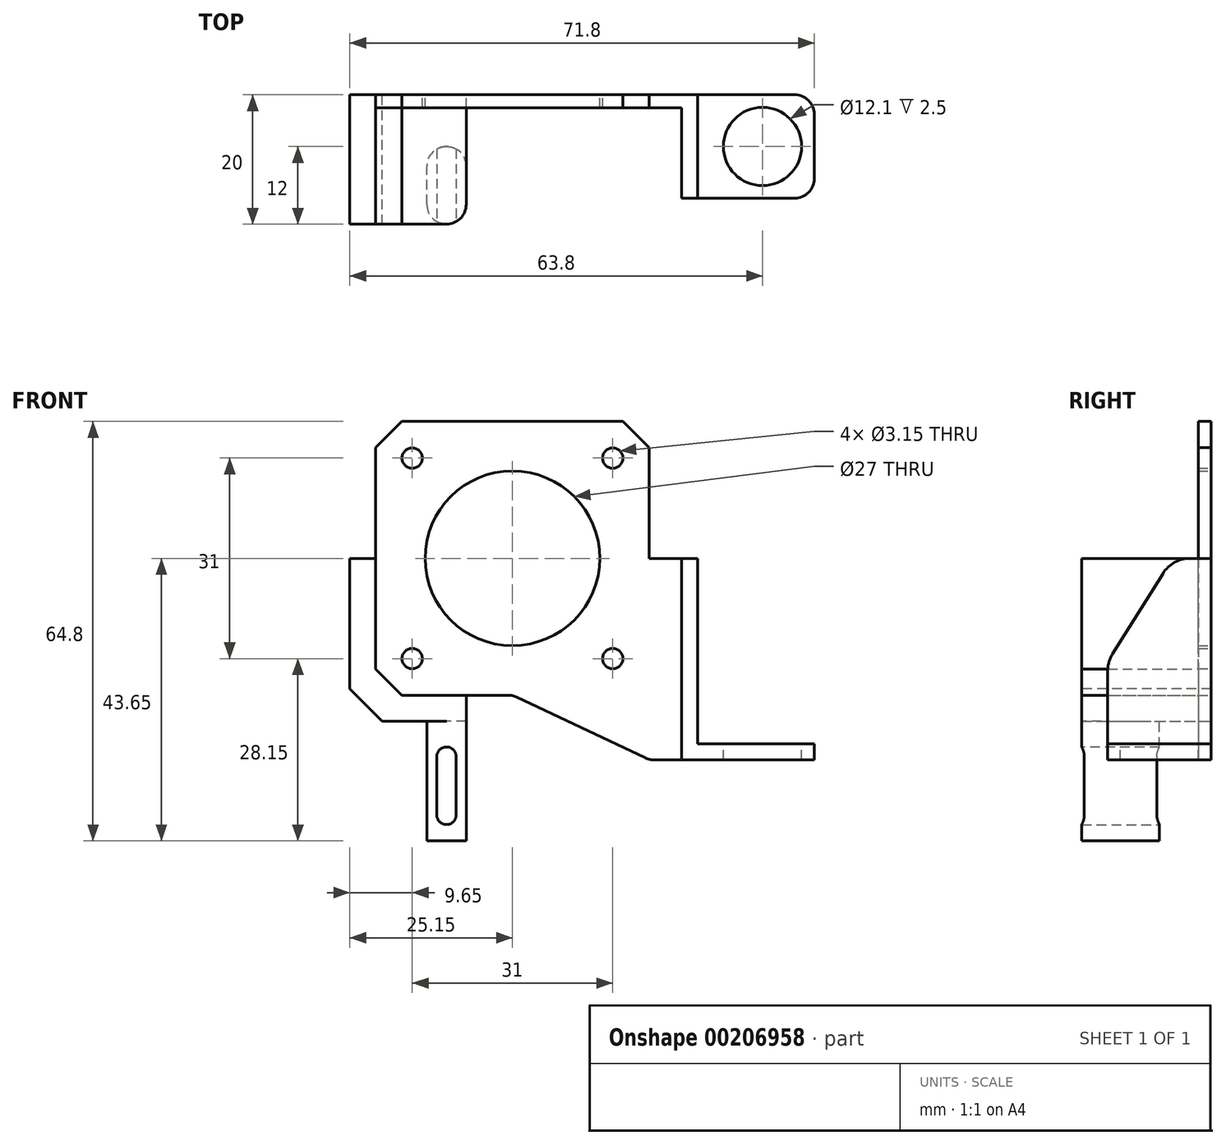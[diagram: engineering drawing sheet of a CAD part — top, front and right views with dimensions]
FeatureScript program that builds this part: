
annotation { "Feature Type Name" : "Feature", "Feature Type Description" : "" }
export const myFeature = defineFeature(function(context is Context, id is Id, definition is map)
    precondition{}
    {
        {
            var Q0;
            Q0=qCreatedBy(makeId("Front.planeOp"),FACE);
            var sketch = newSketch(context, id + "F0", { "sketchPlane" : qUnion([Q0])});
            skLineSegment(sketch, "E0.bottom", {"start": v(21.15, 21.15) * mm, "end": v(-21.15, 21.15) * mm});
            skLineSegment(sketch, "E0.top", {"start": v(21.15, -21.15) * mm, "end": v(-21.15, -21.15) * mm});
            skLineSegment(sketch, "E0.left", {"start": v(21.15, 21.15) * mm, "end": v(21.15, -21.15) * mm});
            skLineSegment(sketch, "E0.right", {"start": v(-21.15, 21.15) * mm, "end": v(-21.15, -21.15) * mm});
            skPoint(sketch, "E0.middle", {"position": v(0, 0) * mm});
            skCircle(sketch, "E1", {"center": v(0, 0) * mm, "radius": 13.5 * mm});
            skCircle(sketch, "E2", {"center": v(-15.5, 15.5) * mm, "radius": 1.57 * mm});
            skCircle(sketch, "E3.MirrorC", {"center": v(15.5, 15.5) * mm, "radius": 1.57 * mm});
            skCircle(sketch, "E4.MirrorC", {"center": v(-15.5, -15.5) * mm, "radius": 1.57 * mm});
            skCircle(sketch, "E5.MirrorC", {"center": v(15.5, -15.5) * mm, "radius": 1.57 * mm});
            skLineSegment(sketch, "E6", {"start": v(-21.15, 0) * mm, "end": v(-25.15, 0) * mm});
            skLineSegment(sketch, "E7", {"start": v(-25.15, 0) * mm, "end": v(-25.15, -25.15) * mm});
            skLineSegment(sketch, "E8", {"start": v(-7.15, -21.15) * mm, "end": v(-7.15, -25.15) * mm});
            skLineSegment(sketch, "E9", {"start": v(-17.08, 21.15) * mm, "end": v(-21.15, 17.08) * mm});
            skLineSegment(sketch, "E10.MirrorCS", {"start": v(17.08, 21.15) * mm, "end": v(21.15, 17.08) * mm});
            skLineSegment(sketch, "E11", {"start": v(-25.15, -25.15) * mm, "end": v(-7.15, -25.15) * mm});
            skLineSegment(sketch, "E12.MirrorCS", {"start": v(-17.08, -21.15) * mm, "end": v(-21.15, -17.08) * mm});
            skLineSegment(sketch, "E13", {"start": v(0, -21.15) * mm, "end": v(21.2, -31.15) * mm});
            skLineSegment(sketch, "E14", {"start": v(21.2, -31.15) * mm, "end": v(46.65, -31.15) * mm});
            skLineSegment(sketch, "E15", {"start": v(46.65, -31.15) * mm, "end": v(46.65, -28.65) * mm});
            skLineSegment(sketch, "E16", {"start": v(46.65, -28.65) * mm, "end": v(28.65, -28.65) * mm});
            skLineSegment(sketch, "E17", {"start": v(28.65, -28.65) * mm, "end": v(28.65, 0) * mm});
            skLineSegment(sketch, "E18", {"start": v(21.15, 0) * mm, "end": v(28.65, 0) * mm});
            skLineSegment(sketch, "E19", {"start": v(26.15, -31.15) * mm, "end": v(26.15, 0) * mm});
            skLineSegment(sketch, "E20", {"start": v(21.15, -21.15) * mm, "end": v(26.15, -21.15) * mm});
            skSolve(sketch);
        }
        {
            var Q0;
            {var subQ1=sQuery(id+"F0.wireOp",EDGE,"wdIhQOyr-LbOw-H7ru-rsnz-cjuyuC4DagCl");Q0=makeQuery(id+"F0.imprint","IMPRINT",FACE,{"disambiguationData":[TD([[makeQuery(id+"F0.imprint","IMPRINT",EDGE,{"derivedFrom":subQ1}),1.0]])]});}
            var Q1;
            {var subQ6=sQuery(id+"F0.wireOp",EDGE,"E6");Q1=makeQuery(id+"F0.imprint","IMPRINT",FACE,{"disambiguationData":[TD([[makeQuery(id+"F0.imprint","IMPRINT",EDGE,{"derivedFrom":subQ6}),1.0]])]});}
            var Q2;
            {var subQ3=sQuery(id+"F0.wireOp",EDGE,"GB1PjnFZ-qV7y-NF51-fnbe-eRyrRNSTYp6C");Q2=makeQuery(id+"F0.imprint","IMPRINT",FACE,{"disambiguationData":[TD([[makeQuery(id+"F0.imprint","IMPRINT",EDGE,{"derivedFrom":subQ3}),1.0]])]});}
            var Q3;
            Q3=makeQuery(id+"F0.imprint","IMPRINT",FACE,{"disambiguationData":[TD([[makeQuery(id+"F0.imprint","IMPRINT",EDGE,{"derivedFrom":sQuery(id+"F0.wireOp",EDGE,"E1")}),-1.0]])]});
            var Q4;
            {var subQ3=sQuery(id+"F0.wireOp",EDGE,"E12.MirrorCS");Q4=makeQuery(id+"F0.imprint","IMPRINT",FACE,{"disambiguationData":[TD([[makeQuery(id+"F0.imprint","IMPRINT",EDGE,{"derivedFrom":subQ3}),1.0]])]});}
            var Q5;
            {var subQ1=sQuery(id+"F0.wireOp",EDGE,"E13");Q5=makeQuery(id+"F0.imprint","IMPRINT",FACE,{"disambiguationData":[TD([[makeQuery(id+"F0.imprint","IMPRINT",EDGE,{"derivedFrom":subQ1}),1.0]])]});}
            var Q6;
            {var subQ1=sQuery(id+"F0.wireOp",EDGE,"E15");Q6=makeQuery(id+"F0.imprint","IMPRINT",FACE,{"disambiguationData":[TD([[makeQuery(id+"F0.imprint","IMPRINT",EDGE,{"derivedFrom":subQ1}),1.0]])]});}
            var Q7;
            {var subQ0=sQuery(id+"F0.wireOp",EDGE,"E20");Q7=makeQuery(id+"F0.imprint","IMPRINT",FACE,{"disambiguationData":[TD([[makeQuery(id+"F0.imprint","IMPRINT",EDGE,{"derivedFrom":subQ0}),1.0]])]});}
            extrude(context, id + "F1", {"entities" : qUnion([Q0, Q1, Q2, Q3, Q4, Q5, Q6, Q7]), "depth" : 2 * mm});
        }
        {
            var Q0;
            {var subQ6=sQuery(id+"F0.wireOp",EDGE,"E6");Q0=makeQuery(id+"F0.imprint","IMPRINT",FACE,{"disambiguationData":[TD([[makeQuery(id+"F0.imprint","IMPRINT",EDGE,{"derivedFrom":subQ6}),1.0]])]});}
            var Q1;
            {var subQ3=sQuery(id+"F0.wireOp",EDGE,"E12.MirrorCS");Q1=makeQuery(id+"F0.imprint","IMPRINT",FACE,{"disambiguationData":[TD([[makeQuery(id+"F0.imprint","IMPRINT",EDGE,{"derivedFrom":subQ3}),1.0]])]});}
            extrude(context, id + "F2", {"entities" : qUnion([Q0, Q1]), "operationType" : NewBodyOperationType.ADD, "depth" : 20 * mm});
        }
        {
            var Q0;
            {var subQ1=sQuery(id+"F0.wireOp",EDGE,"E15");Q0=makeQuery(id+"F0.imprint","IMPRINT",FACE,{"disambiguationData":[TD([[makeQuery(id+"F0.imprint","IMPRINT",EDGE,{"derivedFrom":subQ1}),1.0]])]});}
            extrude(context, id + "F3", {"entities" : qUnion([Q0]), "operationType" : NewBodyOperationType.ADD, "depth" : 16 * mm});
        }
        {
            var Q0;
            {var subQ0=sQuery(id+"F0.wireOp",EDGE,"E16");Q0=makeQuery(id+"F3.boolean.opBoolean","MERGE",FACE,{"derivedFrom":[makeQuery(id+"F1.opExtrude","SWEPT_FACE",FACE,{"disambiguationData":[OSD([subQ0])]}),makeQuery(id+"F3.opExtrude","SWEPT_FACE",FACE,{"disambiguationData":[OSD([subQ0])]})]});}
            var sketch = newSketch(context, id + "F4", { "sketchPlane" : qUnion([Q0])});
            skCircle(sketch, "E21", {"center": v(38.65, -8) * mm, "radius": 6.05 * mm});
            skSolve(sketch);
        }
        {
            var Q0;
            Q0 = qSketchRegion(id + "F4", true);
            extrude(context, id + "F5", {"entities" : qUnion([Q0]), "operationType" : NewBodyOperationType.REMOVE, "endBound" : BoundingType.UP_TO_NEXT, "oppositeDirection" : true, "depth" : 25 * mm});
        }
        {
            var Q0;
            {var subQ0=sQuery(id+"F0.wireOp",EDGE,"E11");Q0=makeQuery(id+"F2.boolean.opBoolean","MERGE",FACE,{"derivedFrom":[makeQuery(id+"F1.opExtrude","SWEPT_FACE",FACE,{"disambiguationData":[OSD([subQ0])]}),makeQuery(id+"F2.opExtrude","SWEPT_FACE",FACE,{"disambiguationData":[OSD([subQ0])]})]});}
            var sketch = newSketch(context, id + "F6", { "sketchPlane" : qUnion([Q0])});
            skLineSegment(sketch, "E22", {"start": v(-13.25, 20) * mm, "end": v(-13.25, 8) * mm});
            skLineSegment(sketch, "E23", {"start": v(-13.25, 8) * mm, "end": v(-7.15, 8) * mm});
            skSolve(sketch);
        }
        {
            var Q0;
            Q0 = qSketchRegion(id + "F6", true);
            var Q1;
            {var subQ0=sQuery(id+"F6.wireOp",EDGE,"E22");Q1=makeQuery(id+"F6.imprint","IMPRINT",FACE,{"disambiguationData":[TD([[makeQuery(id+"F6.imprint","IMPRINT",EDGE,{"derivedFrom":subQ0}),1.0]])]});}
            extrude(context, id + "F7", {"entities" : qUnion([Q0, Q1]), "operationType" : NewBodyOperationType.ADD, "depth" : 18.5 * mm});
        }
        {
            var Q0;
            {var subQ0=sQuery(id+"F0.wireOp",EDGE,"E11");Q0=makeQuery(id+"F7.boolean.opBoolean","MERGE",FACE,{"derivedFrom":[makeQuery(id+"F2.opExtrude","CAP_FACE",FACE,{"disambiguationData":[OSD([sQuery(id+"F0.wireOp",EDGE,"E0.top"),sQuery(id+"F0.wireOp",EDGE,"E0.right"),sQuery(id+"F0.wireOp",EDGE,"E6"),sQuery(id+"F0.wireOp",EDGE,"E7"),sQuery(id+"F0.wireOp",EDGE,"E8"),subQ0,sQuery(id+"F0.wireOp",EDGE,"E12.MirrorCS")])],"isStart":false}),makeQuery(id+"F7.opExtrude","SWEPT_FACE",FACE,{"disambiguationData":[OSD([subQ0])]})]});}
            var sketch = newSketch(context, id + "F8", { "sketchPlane" : qUnion([Q0])});
            skLineSegment(sketch, "E24.bottom", {"start": v(-11.7, -29.15) * mm, "end": v(-8.7, -29.15) * mm});
            skLineSegment(sketch, "E24.top", {"start": v(-11.7, -41.15) * mm, "end": v(-8.7, -41.15) * mm});
            skLineSegment(sketch, "E24.left", {"start": v(-11.7, -29.15) * mm, "end": v(-11.7, -41.15) * mm});
            skLineSegment(sketch, "E24.right", {"start": v(-8.7, -29.15) * mm, "end": v(-8.7, -41.15) * mm});
            skSolve(sketch);
        }
        {
            var Q0;
            Q0 = qSketchRegion(id + "F8", true);
            extrude(context, id + "F9", {"entities" : qUnion([Q0]), "operationType" : NewBodyOperationType.REMOVE, "endBound" : BoundingType.UP_TO_NEXT, "oppositeDirection" : true, "depth" : 25 * mm});
        }
        {
            var Q0;
            Q0=makeQuery(id+"F7.opExtrude","SWEPT_EDGE",EDGE,{"disambiguationData":[OSD([sQuery(id+"F6.wireOp",EDGE,"E22"),sQuery(id+"F6.wireOp",EDGE,"E23")])]});
            var Q1;
            Q1=makeQuery(id+"F7.opExtrude","SWEPT_EDGE",EDGE,{"disambiguationData":[OSD([sQuery(id+"F0.wireOp",EDGE,"E8"),sQuery(id+"F0.wireOp",EDGE,"E11"),sQuery(id+"F6.wireOp",EDGE,"E23")])]});
            var Q2;
            {var subQ0=sQuery(id+"F0.wireOp",EDGE,"E8");Q2=makeQuery(id+"F7.boolean.opBoolean","MERGE",EDGE,{"derivedFrom":[makeQuery(id+"F2.opExtrude","CAP_EDGE",EDGE,{"disambiguationData":[OSD([subQ0])],"isStart":false}),makeQuery(id+"F7.opExtrude","SWEPT_EDGE",EDGE,{"disambiguationData":[OSD([subQ0,sQuery(id+"F0.wireOp",EDGE,"E11")])]})]});}
            var Q3;
            Q3=makeQuery(id+"F7.opExtrude","SWEPT_EDGE",EDGE,{"disambiguationData":[OSD([sQuery(id+"F0.wireOp",EDGE,"E11"),sQuery(id+"F6.wireOp",EDGE,"E22")])]});
            var Q4;
            Q4=makeQuery(id+"F3.opExtrude","CAP_EDGE",EDGE,{"disambiguationData":[OSD([sQuery(id+"F0.wireOp",EDGE,"wdIhQOyr-LbOw-H7ru-rsnz-cjuyuC4DagCl")])],"isStart":false});
            var Q5;
            Q5=makeQuery(id+"F1.opExtrude","CAP_EDGE",EDGE,{"disambiguationData":[OSD([sQuery(id+"F0.wireOp",EDGE,"wdIhQOyr-LbOw-H7ru-rsnz-cjuyuC4DagCl")])],"isStart":true});
            var Q6;
            Q6=makeQuery(id+"F3.opExtrude","CAP_EDGE",EDGE,{"disambiguationData":[OSD([sQuery(id+"F0.wireOp",EDGE,"E15")])],"isStart":false});
            var Q7;
            Q7=makeQuery(id+"F1.opExtrude","CAP_EDGE",EDGE,{"disambiguationData":[OSD([sQuery(id+"F0.wireOp",EDGE,"E15")])],"isStart":true});
            var Q8;
            Q8=makeQuery(id+"F1.opExtrude","SWEPT_EDGE",EDGE,{"disambiguationData":[OSD([sQuery(id+"F0.wireOp",EDGE,"E13"),sQuery(id+"F0.wireOp",EDGE,"E14")])]});
            var Q9;
            Q9=makeQuery(id+"F1.opExtrude","SWEPT_EDGE",EDGE,{"disambiguationData":[OSD([sQuery(id+"F0.wireOp",EDGE,"E0.top"),sQuery(id+"F0.wireOp",EDGE,"E13")])]});
            fillet(context, id + "F10", {"entities" : qUnion([Q0, Q1, Q2, Q3, Q4, Q5, Q6, Q7, Q8, Q9]), "radius" : 3.05 * mm, "tangentPropagation" : true, "allowEdgeOverflow" : false});
        }
        {
            var Q0;
            Q0=makeQuery(id+"F9.boolean.opBoolean","COPY",EDGE,{"derivedFrom":makeQuery(id+"F9.opExtrude","SWEPT_EDGE",EDGE,{"disambiguationData":[OSD([sQuery(id+"F8.wireOp",EDGE,"E24.bottom"),sQuery(id+"F8.wireOp",EDGE,"E24.left")])]})});
            var Q1;
            Q1=makeQuery(id+"F9.boolean.opBoolean","COPY",EDGE,{"derivedFrom":makeQuery(id+"F9.opExtrude","SWEPT_EDGE",EDGE,{"disambiguationData":[OSD([sQuery(id+"F8.wireOp",EDGE,"E24.bottom"),sQuery(id+"F8.wireOp",EDGE,"E24.right")])]})});
            var Q2;
            Q2=makeQuery(id+"F9.boolean.opBoolean","COPY",EDGE,{"derivedFrom":makeQuery(id+"F9.opExtrude","SWEPT_EDGE",EDGE,{"disambiguationData":[OSD([sQuery(id+"F8.wireOp",EDGE,"E24.top"),sQuery(id+"F8.wireOp",EDGE,"E24.left")])]})});
            var Q3;
            Q3=makeQuery(id+"F9.boolean.opBoolean","COPY",EDGE,{"derivedFrom":makeQuery(id+"F9.opExtrude","SWEPT_EDGE",EDGE,{"disambiguationData":[OSD([sQuery(id+"F8.wireOp",EDGE,"E24.top"),sQuery(id+"F8.wireOp",EDGE,"E24.right")])]})});
            var Q4;
            {var subQ0=sQuery(id+"F0.wireOp",EDGE,"Ab5imJkb-bv9U-3p64-btrf-NdYsAKqCKsP3");var subQ1=sQuery(id+"F0.wireOp",EDGE,"1rr1lGT1-vjx1-utsH-0JqL-JJ0WfiPwg6K2");Q4=makeQuery(id+"F3.boolean.opBoolean","MERGE",EDGE,{"derivedFrom":[makeQuery(id+"F1.opExtrude","SWEPT_EDGE",EDGE,{"disambiguationData":[OSD([subQ1,subQ0])]}),makeQuery(id+"F3.opExtrude","SWEPT_EDGE",EDGE,{"disambiguationData":[OSD([subQ1,subQ0])]})]});}
            var Q5;
            Q5=makeQuery(id+"F3.opExtrude","SWEPT_EDGE",EDGE,{"disambiguationData":[OSD([sQuery(id+"F0.wireOp",EDGE,"Tm5QZafz-MtUj-E81s-fdnC-w6Kw9Eq9n858"),sQuery(id+"F0.wireOp",EDGE,"9ylnEtLT-uUGL-5WkY-GiLn-3v2g5TGhLVdF")])]});
            fillet(context, id + "F11", {"entities" : qUnion([Q0, Q1, Q2, Q3, Q4, Q5]), "radius" : 1.5 * mm, "tangentPropagation" : true, "allowEdgeOverflow" : false});
        }
        {
            var Q0;
            {var subQ0=sQuery(id+"F0.wireOp",EDGE,"E11");var subQ1=sQuery(id+"F0.wireOp",EDGE,"E7");Q0=makeQuery(id+"F2.boolean.opBoolean","MERGE",EDGE,{"derivedFrom":[makeQuery(id+"F1.opExtrude","SWEPT_EDGE",EDGE,{"disambiguationData":[OSD([subQ1,subQ0])]}),makeQuery(id+"F2.opExtrude","SWEPT_EDGE",EDGE,{"disambiguationData":[OSD([subQ1,subQ0])]})]});}
            chamfer(context, id + "F12", {"entities" : qUnion([Q0]), "width" : 5 * mm, "tangentPropagation" : true});
        }
        {
            var Q0;
            Q0=makeQuery(id+"F3.opExtrude","CAP_EDGE",EDGE,{"disambiguationData":[OSD([sQuery(id+"F0.wireOp",EDGE,"E18")])],"isStart":false});
            chamfer(context, id + "F13", {"entities" : qUnion([Q0]), "chamferType" : ChamferType.TWO_OFFSETS, "width1" : 10 * mm, "oppositeDirection" : false, "width2" : 16 * mm, "tangentPropagation" : true});
        }
        {
            var Q0;
            {var subQ0=sQuery(id+"F0.wireOp",EDGE,"E18");Q0=makeQuery(id+"F13.opChamfer","BLEND_EDGE",EDGE,{"blendedFrom":[makeQuery(id+"F3.opExtrude","CAP_EDGE",EDGE,{"disambiguationData":[OSD([subQ0])],"isStart":false}),makeQuery(id+"F3.opExtrude","CAP_FACE",FACE,{"disambiguationData":[OSD([sQuery(id+"F0.wireOp",EDGE,"E14"),sQuery(id+"F0.wireOp",EDGE,"E15"),sQuery(id+"F0.wireOp",EDGE,"E16"),sQuery(id+"F0.wireOp",EDGE,"E17"),subQ0,sQuery(id+"F0.wireOp",EDGE,"E19")])],"isStart":false})],"blendedInto":[makeQuery(id+"F3.opExtrude","CAP_FACE",FACE,{"disambiguationData":[OSD([sQuery(id+"F0.wireOp",EDGE,"E14"),sQuery(id+"F0.wireOp",EDGE,"E15"),sQuery(id+"F0.wireOp",EDGE,"E16"),sQuery(id+"F0.wireOp",EDGE,"E17"),subQ0,sQuery(id+"F0.wireOp",EDGE,"E19")])],"isStart":false})]});}
            var Q1;
            {var subQ0=sQuery(id+"F0.wireOp",EDGE,"E18");Q1=makeQuery(id+"F13.opChamfer","BLEND_EDGE",EDGE,{"blendedFrom":[makeQuery(id+"F3.opExtrude","CAP_EDGE",EDGE,{"disambiguationData":[OSD([subQ0])],"isStart":false}),makeQuery(id+"F3.boolean.opBoolean","MERGE",FACE,{"derivedFrom":[makeQuery(id+"F1.opExtrude","SWEPT_FACE",FACE,{"disambiguationData":[OSD([subQ0])]}),makeQuery(id+"F3.opExtrude","SWEPT_FACE",FACE,{"disambiguationData":[OSD([subQ0])]})]})],"blendedInto":[makeQuery(id+"F3.boolean.opBoolean","MERGE",FACE,{"derivedFrom":[makeQuery(id+"F1.opExtrude","SWEPT_FACE",FACE,{"disambiguationData":[OSD([subQ0])]}),makeQuery(id+"F3.opExtrude","SWEPT_FACE",FACE,{"disambiguationData":[OSD([subQ0])]})]})]});}
            fillet(context, id + "F14", {"entities" : qUnion([Q0, Q1]), "radius" : 5 * mm, "tangentPropagation" : true, "allowEdgeOverflow" : false});
        }
    });
